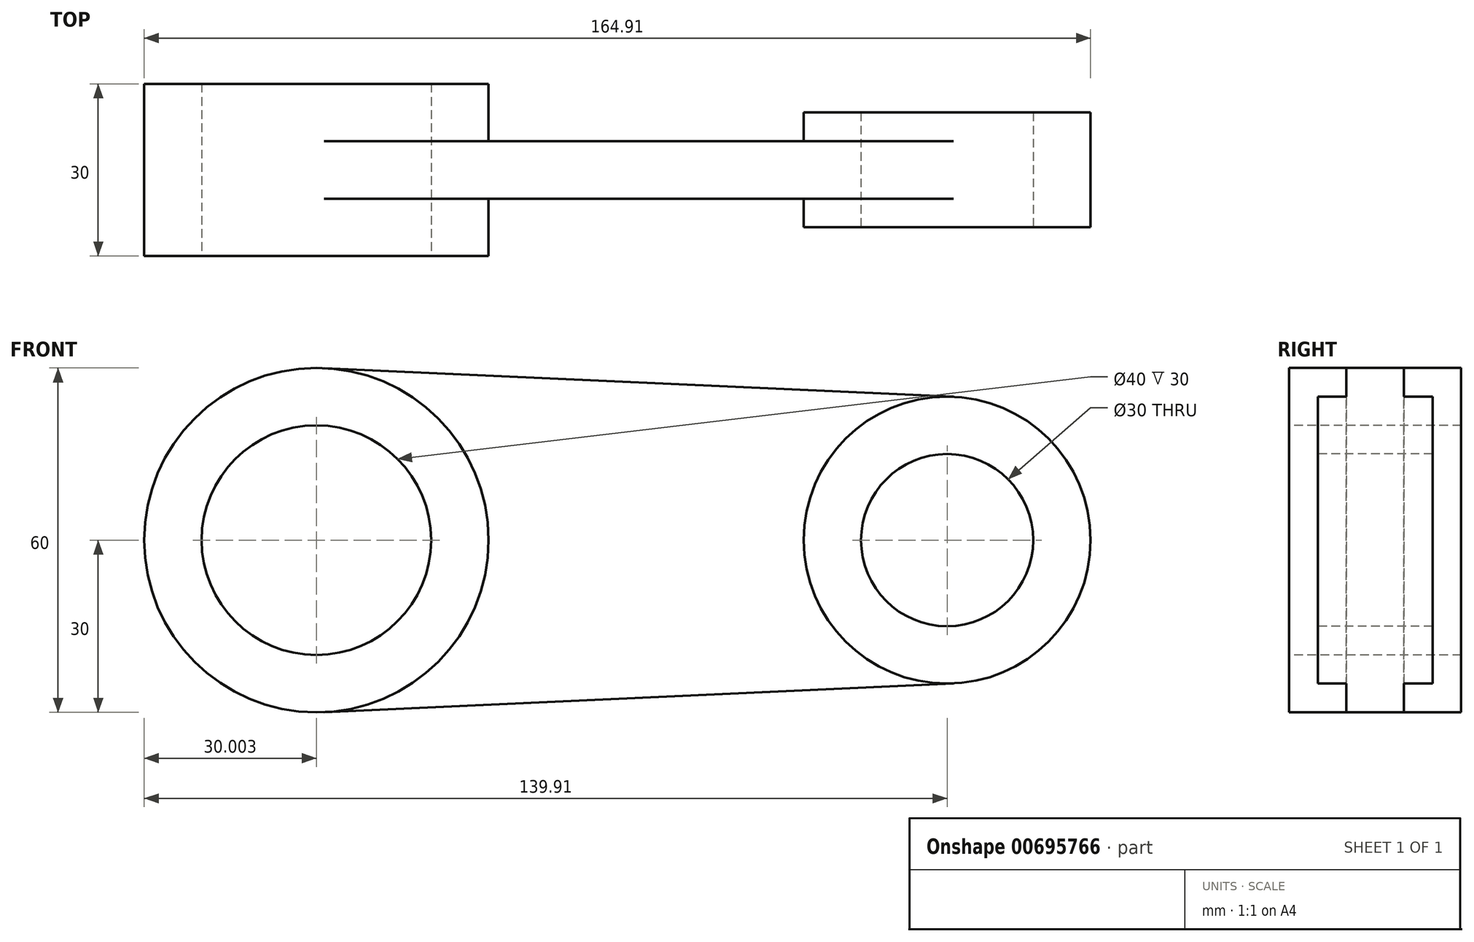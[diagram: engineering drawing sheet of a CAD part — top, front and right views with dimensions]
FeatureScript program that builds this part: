
annotation { "Feature Type Name" : "Feature", "Feature Type Description" : "" }
export const myFeature = defineFeature(function(context is Context, id is Id, definition is map)
    precondition{}
    {
        {
            var Q0;
            Q0=qCreatedBy(makeId("Front.planeOp"),FACE);
            var sketch = newSketch(context, id + "F0", { "sketchPlane" : qUnion([Q0])});
            skCircle(sketch, "E0", {"center": v(-69.26, 0) * mm, "radius": 30 * mm});
            skCircle(sketch, "E1", {"center": v(-69.26, 0) * mm, "radius": 20 * mm});
            skCircle(sketch, "E2", {"center": v(40.65, 0) * mm, "radius": 15 * mm});
            skCircle(sketch, "E3", {"center": v(40.65, 0) * mm, "radius": 25 * mm});
            skLineSegment(sketch, "E4", {"start": v(-67.9, 29.97) * mm, "end": v(41.79, 24.97) * mm});
            skLineSegment(sketch, "E5", {"start": v(-67.9, -29.97) * mm, "end": v(41.79, -24.97) * mm});
            skSolve(sketch);
        }
        {
            var Q0;
            {var subQ0=sQuery(id+"F0.wireOp",EDGE,"E4");Q0=makeQuery(id+"F0.imprint","IMPRINT",FACE,{"disambiguationData":[TD([[makeQuery(id+"F0.imprint","IMPRINT",EDGE,{"derivedFrom":subQ0}),-1.0]])]});}
            extrude(context, id + "F1", {"entities" : qUnion([Q0]), "oppositeDirection" : true, "depth" : 10 * mm, "offsetDistance" : 25 * mm});
        }
        {
            var Q0;
            Q0=makeQuery(id+"F0.imprint","IMPRINT",FACE,{"disambiguationData":[TD([[makeQuery(id+"F0.imprint","IMPRINT",EDGE,{"derivedFrom":sQuery(id+"F0.wireOp",EDGE,"E1")}),-1.0]])]});
            extrude(context, id + "F2", {"entities" : qUnion([Q0]), "operationType" : NewBodyOperationType.ADD, "oppositeDirection" : true, "depth" : 20 * mm, "offsetDistance" : 25 * mm});
        }
        {
            var Q0;
            Q0=makeQuery(id+"F0.imprint","IMPRINT",FACE,{"disambiguationData":[TD([[makeQuery(id+"F0.imprint","IMPRINT",EDGE,{"derivedFrom":sQuery(id+"F0.wireOp",EDGE,"E2")}),-1.0]])]});
            extrude(context, id + "F3", {"entities" : qUnion([Q0]), "oppositeDirection" : true, "depth" : 15 * mm, "offsetDistance" : 25 * mm});
        }
        {
            var Q0;
            Q0=makeQuery(id+"F0.imprint","IMPRINT",FACE,{"disambiguationData":[TD([[makeQuery(id+"F0.imprint","IMPRINT",EDGE,{"derivedFrom":sQuery(id+"F0.wireOp",EDGE,"E1")}),-1.0]])]});
            extrude(context, id + "F4", {"entities" : qUnion([Q0]), "operationType" : NewBodyOperationType.ADD, "depth" : 10 * mm, "offsetDistance" : 25 * mm});
        }
        {
            var Q0;
            Q0=makeQuery(id+"F0.imprint","IMPRINT",FACE,{"disambiguationData":[TD([[makeQuery(id+"F0.imprint","IMPRINT",EDGE,{"derivedFrom":sQuery(id+"F0.wireOp",EDGE,"E2")}),-1.0]])]});
            extrude(context, id + "F5", {"entities" : qUnion([Q0]), "operationType" : NewBodyOperationType.ADD, "depth" : 5 * mm, "offsetDistance" : 25 * mm});
        }
    });
